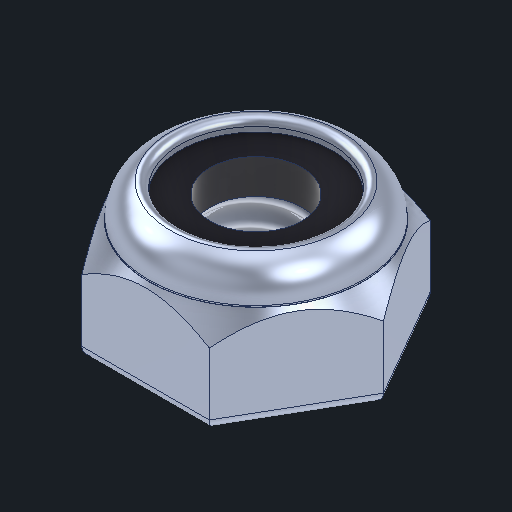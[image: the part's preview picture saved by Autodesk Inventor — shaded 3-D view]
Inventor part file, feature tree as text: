
AUTODESK INVENTOR PART (.ipt)
format: ipt  version: 2024 (Build 280153000, 153)  size: 228,864 bytes
history: native  units: in
note: dims shown in document units (in); Inventor stores cm internally (conversion verified against a paired STEP export)
features: other x4, sketch x2, plane x1
ambient origin geometry x8: Origin, YZ Plane, XZ Plane, XY Plane, X Axis, Y Axis, Z Axis, Center Point
bodies: Body1 (feature_tree)
feature tree (7):
  other  "Nut Thin Nylock.ipt"
  other  "NONE::Nut Thin Nylock.ipt"
  other  "TaggingFeature1"
  sketch  "Sketch1"  dims[d0=0.3937in]
  sketch  "Sketch2"
  plane  "Work Plane1"
  parser-record x1  (decoder bookkeeping rows leaked as tree rows — omitted from the tree; the rows remain in map.json)
